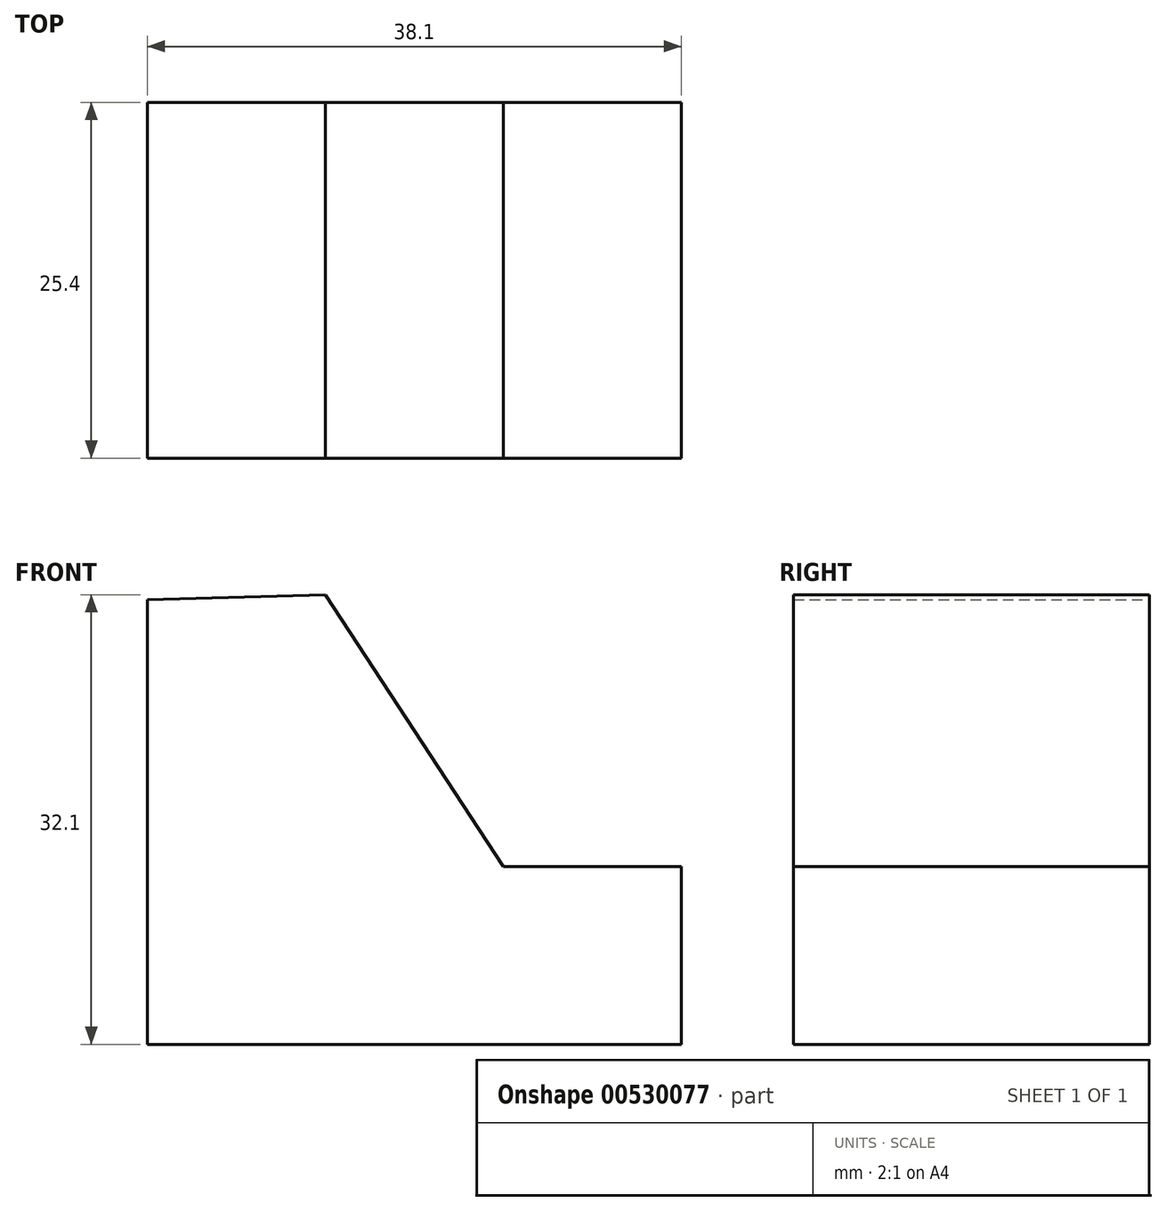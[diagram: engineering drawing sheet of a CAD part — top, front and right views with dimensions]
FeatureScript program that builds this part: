
annotation { "Feature Type Name" : "Feature", "Feature Type Description" : "" }
export const myFeature = defineFeature(function(context is Context, id is Id, definition is map)
    precondition{}
    {
        {
            var Q0;
            Q0=qCreatedBy(makeId("Front.planeOp"),FACE);
            var sketch = newSketch(context, id + "F0", { "sketchPlane" : qUnion([Q0])});
            skLineSegment(sketch, "E0", {"start": v(-62.06, 42.5) * mm, "end": v(-62.06, 10.76) * mm});
            skLineSegment(sketch, "E1", {"start": v(-62.06, 10.76) * mm, "end": v(-23.96, 10.76) * mm});
            skLineSegment(sketch, "E2", {"start": v(-23.96, 10.76) * mm, "end": v(-23.96, 23.46) * mm});
            skLineSegment(sketch, "E3", {"start": v(-23.96, 23.46) * mm, "end": v(-36.66, 23.46) * mm});
            skLineSegment(sketch, "E4", {"start": v(-36.66, 23.46) * mm, "end": v(-49.37, 42.86) * mm});
            skLineSegment(sketch, "E5", {"start": v(-49.37, 42.86) * mm, "end": v(-62.06, 42.5) * mm});
            skSolve(sketch);
        }
        {
            var Q0;
            Q0=makeQuery(id+"F0.imprint","IMPRINT",FACE,{"disambiguationData":[TD([[makeQuery(id+"F0.imprint","IMPRINT",EDGE,{"derivedFrom":sQuery(id+"F0.wireOp",EDGE,"E0")}),1.0]])]});
            extrude(context, id + "F1", {"entities" : qUnion([Q0]), "depth" : 25.4 * mm, "offsetDistance" : 25.4 * mm});
        }
    });
